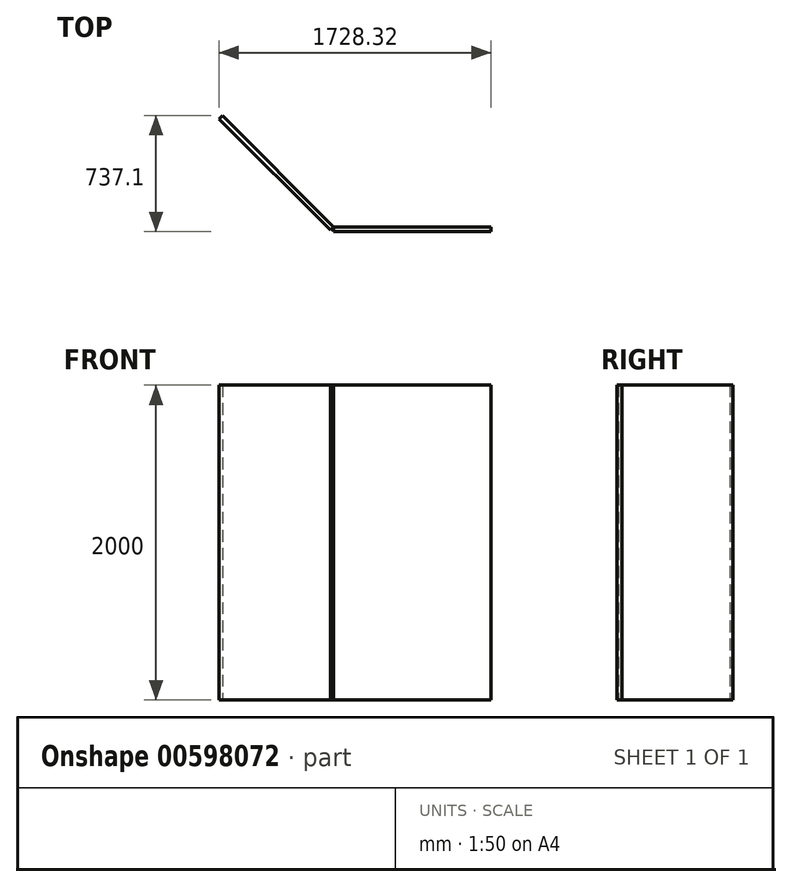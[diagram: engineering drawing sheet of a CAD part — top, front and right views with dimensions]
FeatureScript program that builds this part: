
annotation { "Feature Type Name" : "Feature", "Feature Type Description" : "" }
export const myFeature = defineFeature(function(context is Context, id is Id, definition is map)
    precondition{}
    {
        {
            var Q0;
            Q0=qCreatedBy(makeId("Top.planeOp"),FACE);
            var sketch = newSketch(context, id + "F0", { "sketchPlane" : qUnion([Q0])});
            skLineSegment(sketch, "E0.bottom", {"start": v(-156.9, -228.84) * mm, "end": v(843.1, -228.84) * mm});
            skLineSegment(sketch, "E0.top", {"start": v(-156.9, -258.84) * mm, "end": v(843.1, -258.84) * mm});
            skLineSegment(sketch, "E0.left", {"start": v(-156.9, -228.84) * mm, "end": v(-156.9, -258.84) * mm});
            skLineSegment(sketch, "E0.right", {"start": v(843.1, -228.84) * mm, "end": v(843.1, -258.84) * mm});
            skLineSegment(sketch, "E1", {"start": v(-156.9, -228.84) * mm, "end": v(-864.01, 478.26) * mm});
            skLineSegment(sketch, "E2", {"start": v(-864.01, 478.26) * mm, "end": v(-885.22, 457.05) * mm});
            skLineSegment(sketch, "E3", {"start": v(-885.22, 457.05) * mm, "end": v(-178.12, -250.06) * mm});
            skLineSegment(sketch, "E4", {"start": v(-178.12, -250.06) * mm, "end": v(-156.9, -228.84) * mm});
            skSolve(sketch);
        }
        {
            var Q0;
            Q0=qSketchRegion(id+"F0",true);
            extrude(context, id + "F1", {"entities" : qUnion([Q0]), "depth" : 2000 * mm, "offsetDistance" : 25 * mm});
        }
    });
